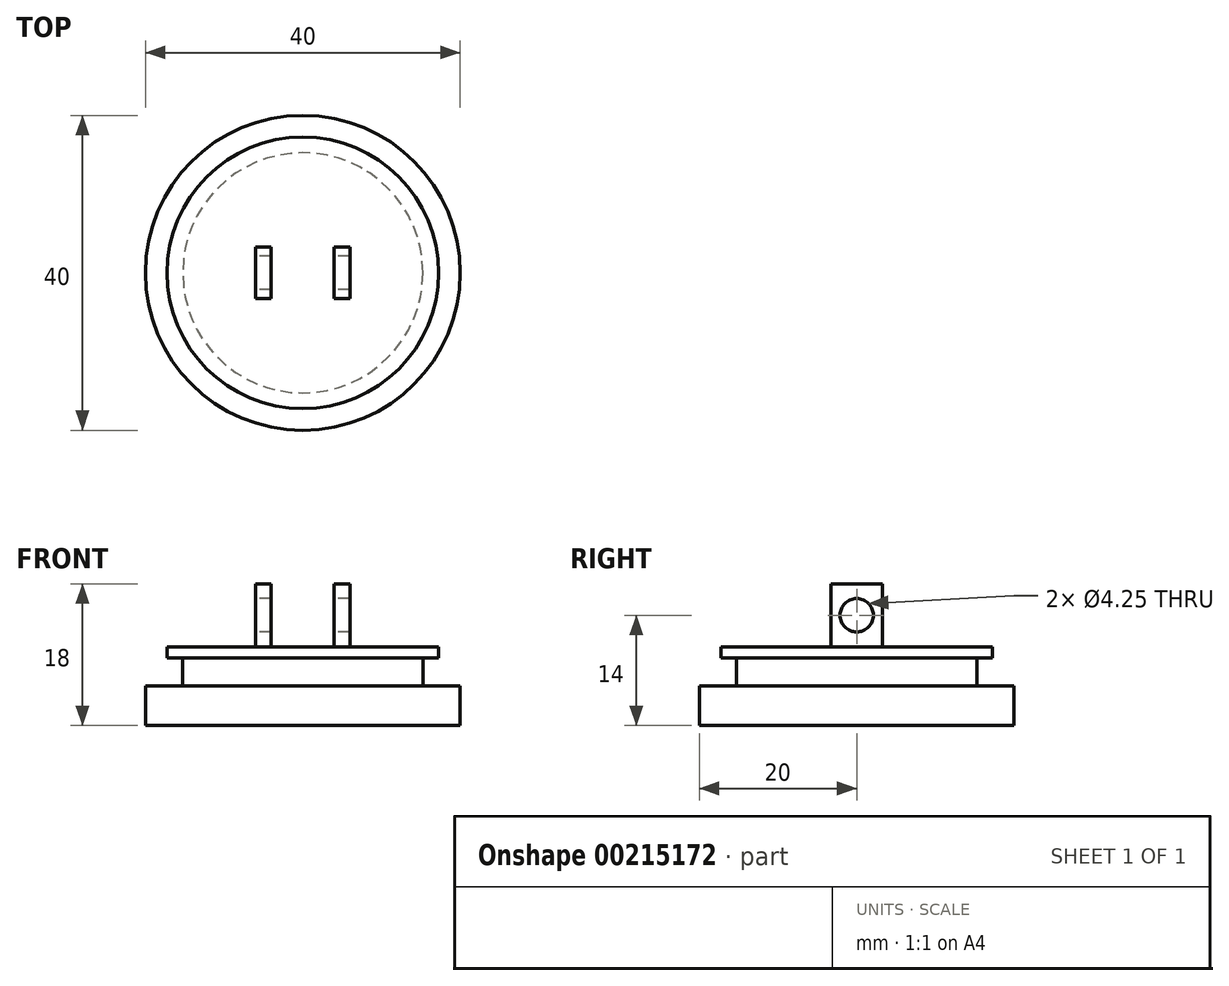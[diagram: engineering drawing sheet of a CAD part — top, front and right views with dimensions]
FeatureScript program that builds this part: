
annotation { "Feature Type Name" : "Feature", "Feature Type Description" : "" }
export const myFeature = defineFeature(function(context is Context, id is Id, definition is map)
    precondition{}
    {
        {
            var Q0;
            Q0=qCreatedBy(makeId("Top.planeOp"),FACE);
            var sketch = newSketch(context, id + "F0", { "sketchPlane" : qUnion([Q0])});
            skCircle(sketch, "E0", {"center": v(0, 0) * mm, "radius": 20 * mm});
            skSolve(sketch);
        }
        {
            var Q0;
            Q0 = qSketchRegion(id + "F0", true);
            extrude(context, id + "F1", {"entities" : qUnion([Q0]), "depth" : 5 * mm});
        }
        {
            var Q0;
            Q0=qCreatedBy(makeId("Top.planeOp"),FACE);
            var sketch = newSketch(context, id + "F2", { "sketchPlane" : qUnion([Q0])});
            skCircle(sketch, "E1", {"center": v(0, 0) * mm, "radius": 17.25 * mm});
            skSolve(sketch);
        }
        {
            var Q0;
            Q0 = qSketchRegion(id + "F2", true);
            extrude(context, id + "F3", {"entities" : qUnion([Q0]), "operationType" : NewBodyOperationType.ADD, "depth" : 10 * mm});
        }
        {
            var Q0;
            Q0=qCreatedBy(makeId("Right.planeOp"),FACE);
            var sketch = newSketch(context, id + "F4", { "sketchPlane" : qUnion([Q0])});
            skLineSegment(sketch, "E2", {"start": v(17.25, 8.56) * mm, "end": v(15.25, 8.56) * mm});
            skLineSegment(sketch, "E3", {"start": v(15.25, 8.56) * mm, "end": v(15.25, 5) * mm});
            skLineSegment(sketch, "E4", {"start": v(15.25, 5) * mm, "end": v(17.25, 5) * mm});
            skLineSegment(sketch, "E5", {"start": v(17.25, 5) * mm, "end": v(17.25, 8.56) * mm});
            skSolve(sketch);
        }
        {
            var Q0;
            Q0=qCreatedBy(makeId("Right.planeOp"),FACE);
            var sketch = newSketch(context, id + "F5", { "sketchPlane" : qUnion([Q0])});
            skLineSegment(sketch, "E6", {"start": v(0, 0) * mm, "end": v(0, 13.64) * mm});
            skSolve(sketch);
        }
        {
            var Q0;
            Q0 = qSketchRegion(id + "F4", true);
            var Q1;
            Q1=sQuery(id+"F5.wireOp",EDGE,"E6");
            revolve(context, id + "F6", {"operationType" : NewBodyOperationType.REMOVE, "entities" : qUnion([Q0]), "axis" : qUnion([Q1]), "revolveType" : RevolveType.FULL, "oppositeDirection" : true});
        }
        {
            var Q0;
            Q0=makeQuery(id+"F3.opExtrude","CAP_FACE",FACE,{"disambiguationData":[OSD([sQuery(id+"F2.wireOp",EDGE,"E1")])],"isStart":false});
            var sketch = newSketch(context, id + "F7", { "sketchPlane" : qUnion([Q0])});
            skLineSegment(sketch, "E7.bottom", {"start": v(6, 3.25) * mm, "end": v(4, 3.25) * mm});
            skLineSegment(sketch, "E7.top", {"start": v(6, -3.25) * mm, "end": v(4, -3.25) * mm});
            skLineSegment(sketch, "E7.left", {"start": v(6, 3.25) * mm, "end": v(6, -3.25) * mm});
            skLineSegment(sketch, "E7.right", {"start": v(4, 3.25) * mm, "end": v(4, -3.25) * mm});
            skPoint(sketch, "E7.middle", {"position": v(5, 0) * mm});
            skLineSegment(sketch, "E8.bottom", {"start": v(-6, 3.25) * mm, "end": v(-4, 3.25) * mm});
            skLineSegment(sketch, "E8.top", {"start": v(-6, -3.25) * mm, "end": v(-4, -3.25) * mm});
            skLineSegment(sketch, "E8.left", {"start": v(-6, 3.25) * mm, "end": v(-6, -3.25) * mm});
            skLineSegment(sketch, "E8.right", {"start": v(-4, 3.25) * mm, "end": v(-4, -3.25) * mm});
            skPoint(sketch, "E8.middle", {"position": v(-5, 0) * mm});
            skSolve(sketch);
        }
        {
            var Q0;
            Q0 = qSketchRegion(id + "F7", true);
            extrude(context, id + "F8", {"entities" : qUnion([Q0]), "operationType" : NewBodyOperationType.ADD, "depth" : 8 * mm});
        }
        {
            var Q0;
            Q0=makeQuery(id+"F8.opExtrude","SWEPT_FACE",FACE,{"disambiguationData":[OSD([sQuery(id+"F7.wireOp",EDGE,"E8.left")])]});
            var sketch = newSketch(context, id + "F9", { "sketchPlane" : qUnion([Q0])});
            skCircle(sketch, "E9", {"center": v(0, 14) * mm, "radius": 2.12 * mm});
            skSolve(sketch);
        }
        {
            var Q0;
            Q0 = qSketchRegion(id + "F9", true);
            extrude(context, id + "F10", {"entities" : qUnion([Q0]), "operationType" : NewBodyOperationType.REMOVE, "endBound" : BoundingType.THROUGH_ALL, "oppositeDirection" : true, "depth" : 25 * mm});
        }
    });
